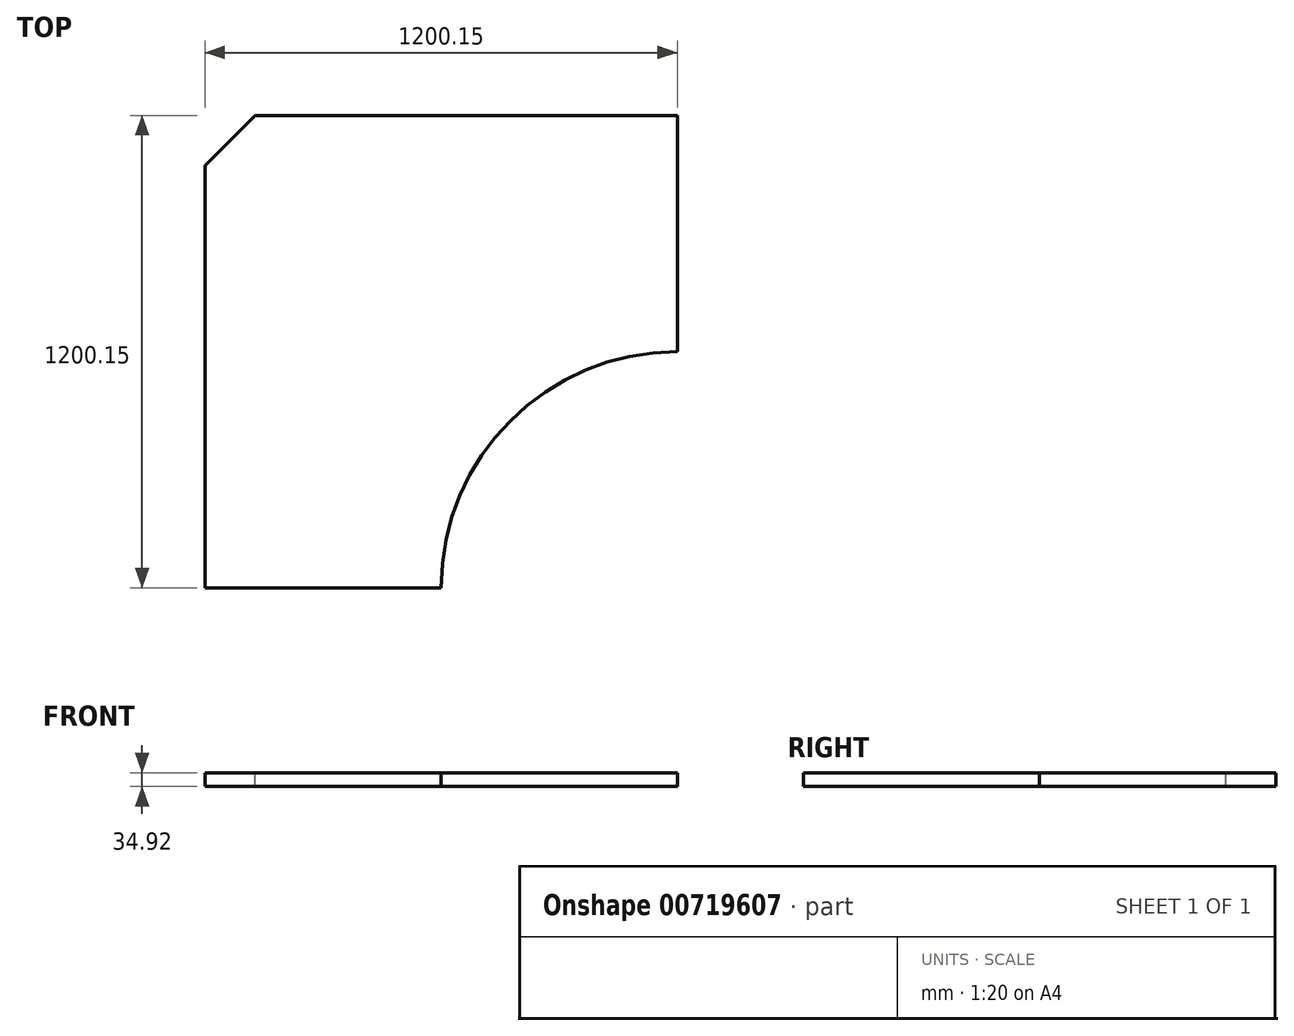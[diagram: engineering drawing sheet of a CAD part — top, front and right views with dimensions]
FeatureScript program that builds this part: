
annotation { "Feature Type Name" : "Feature", "Feature Type Description" : "" }
export const myFeature = defineFeature(function(context is Context, id is Id, definition is map)
    precondition{}
    {
        {
            var Q0;
            Q0=qCreatedBy(makeId("Top.planeOp"),FACE);
            var sketch = newSketch(context, id + "F0", { "sketchPlane" : qUnion([Q0])});
            skLineSegment(sketch, "E0.bottom", {"start": v(127, 0) * mm, "end": v(1200.15, 0) * mm});
            skLineSegment(sketch, "E0.top", {"start": v(0, -1200.15) * mm, "end": v(600.08, -1200.15) * mm});
            skLineSegment(sketch, "E0.left", {"start": v(0, -127) * mm, "end": v(0, -1200.15) * mm});
            skLineSegment(sketch, "E0.right", {"start": v(1200.15, 0) * mm, "end": v(1200.15, -600.07) * mm});
            skArc(sketch, "E1", {"start": v(1200.15, -600.07) * mm, "mid": v(775.83, -775.83) * mm, "end": v(600.08, -1200.15) * mm});
            skLineSegment(sketch, "E2", {"start": v(0, -127) * mm, "end": v(127, 0) * mm});
            skPoint(sketch, "E3.orphan", {"position": v(0, 0) * mm});
            skSolve(sketch);
        }
        {
            var Q0;
            Q0=makeQuery(id+"F0.imprint","IMPRINT",FACE,{"disambiguationData":[TD([[makeQuery(id+"F0.imprint","IMPRINT",EDGE,{"derivedFrom":sQuery(id+"F0.wireOp",EDGE,"E0.bottom")}),-1.0]])]});
            extrude(context, id + "F1", {"entities" : qUnion([Q0]), "oppositeDirection" : true, "depth" : 34.92 * mm, "offsetDistance" : 25.4 * mm});
        }
    });
